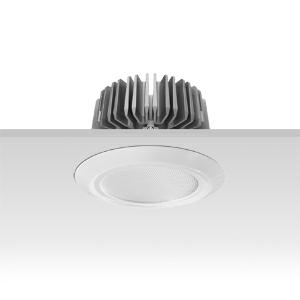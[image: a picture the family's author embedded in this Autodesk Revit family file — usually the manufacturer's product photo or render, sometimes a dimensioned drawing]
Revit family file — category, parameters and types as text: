
# Revit family: 3f_filippi_-_3f_reno_bianco_ampio_3f_filippi_-_30345_a01046_-_3f_reno_150_wh_2000-930_wide___smp_wh_e8fd
name_source: partatom
category: Lighting Fixtures
units: mm (PartAtom-declared; Revit-internal decimal feet)

## family parameters
Cut with Voids When Loaded = No
Host = Face
Light Source = No
Part Type = Normal
Room Calculation Point = No
Round Connector Dimension = Use Diameter
Shared = No

## types (1)
- 3F Filippi - 3F Reno Bianco Ampio (1 x LED, 1652 lm, 24 W, 3000 K)
    Apparent Load = 24 VA
    Approval mark = CE
    CIE Flux Codes = 73 92 98 100 100
    Color Rendering = 90
    Color Temperature = 3000 K
    Control Gear = Electronic ballast
    Default Elevation = 1800 mm
    Description = ILLUMINOTECHNICAL
Luminous efficiency 100% (DLOR 100%, ULOR 0%).
Initial luminous flux of the luminaire 1652 lm.
Direct symmetric wide distribution.
Installation Interdistance Transv.D = 1.01 x hu - Long.D = 1.00 x hu.
Tabular UGR (CIE 117 - 4H-8H; S=0.25H; 70/50/20): RUG 23.3 - 23.3.
Beam angle: 70° - 70°.
Luminous efficacy 69 lm/W.
Lifetime (L90/B10): 30000 h. (tq+25°C)
Lifetime (L85/B10): 50000 h. (tq+25°C)
Lifetime (L70/B10): 80000 h. (tq+25°C)
Sudden decreased luminous flux after 50000 hours: 0% (C0).
Photobiological safety in compliance with IEC/TR 62778: RG0 risk exempt, (IEC 62471).
In compliance with IEC/EN 62722-2-1 - IEC/EN 62717 standards.

SOURCE
Compact LED module 2000/930.
Energy efficiency class (UE 2019/2020 - UE 2019/2015): E.
CIE 13.3 Colour rendering index: CRI >90 (R9 >50%).
IES TM-30 Fidelity Index: Rf = 92 Rg = 101.
CCT nominal colour temperature 3000 K.
Colour initial tolerance (MacAdam): SDCM 3.
Zhaga Book 3 compliant.

MECHANICAL
Passive heat dissipator in die-casting aluminium, oversized, for optimum thermal management of the LED module.
Parabolic element with graduated/concentric rings in white polycarbonate.
Transparent external lens with glossy and satin differentiated surfaces, with a cooling and anti-insect system in methacrylate (PMMA).
Fastening spring clips in stainless steel.
Dimensions: diameter 176 mm, height 111 mm. Weight 0.75 kg.
IP44 protection degree for exposed part, IP20 for recessed part.
Mechanical strength to impacts IK05 (0.7 joule).
Glow-wire test resistance 650°C.

ELECTRICAL
Wiring on a separate unit.
Halogen Free electronic wiring 230V-50/60Hz, power factor 0.95, THD <25%, constant output current, SELV, class II, 1 driver.
Power of the luminaire 24 W.
ENEC - CE.
SAFE FLICKER: PstLM=<1 and SVM=<0.4 (IEC TR 61547-1 and IEC TR 63158), to ensure a more comfortable and safe light.
Luminaire compliant with EN 60598-2-22 for power supply from a centralised emergency system CPSS (Central Power Supply System), not incorporated in the luminaire - high risk areas excluded. The default power and flux are 100% in AC and 100% in DC.
Ambient temperature from 0°C to +25°C.
Temperature class T6 max 85°C.
Relative humidity UR: <85%.

INSTALLATION
Pull-up recessed fitting.
False ceiling carving: 150 mm.
All accessories dedicated to this product are available on the Catalog and on our website www.3F-Filippi.com.

ACCESSORIES
A01046 - Anti-glare microprismatic SMP diffuser in methacrylate (PMMA), locked and in line with the trim, in white polycarbonate.

APPLICATIONS
Suitable product for food production plants (HACCP), IFS (Food Version 6), BRC (GSFS Food Version 7).
Environments: architectural, commercial, exhibition areas, transit areas, corridors, shops, display windows, service areas.
In false ceilings with narrow voids.

WARNING
Luminaire designed for disposal/recycling at end-of-life.
Replaceable (LED only) light source by a professional. Replaceable control gear by a professional.
    Height = 0 mm  [stored 0 ft]
    Lamp = 1 x LED
    Lamp Light Flux = 1652 lm
    Lamp Power = 24 W
    Lamp count = 1
    Length = 176 mm
    Lifetime = 50000 h
    Luminous efficacy = 69 lm/W
    Manufacturer = 3F Filippi
    ModVariant = No
    Model = 3F Filippi - 30345+A01046 - 3F Reno 150 WH 2000-930 WIDE + SMP WH
    Mounting Place = Ceiling
    Mounting Type = Recessed
    Number of Poles = 1
    OnlyDefault = Yes
    Power Factor = 1
    Product Name = 3F Filippi - 3F Reno Bianco Ampio
    Product group = recessed luminaire
    ProductGroupID = 4
    Protection Class = Protection class II
    Protection Degree = IP 20
    RLX_Detail_Level = 1
    RLX_Emergency_Light_Flux = 0 lm
    RLX_Emergency_Type = 0
    RLX_Emergency_Type_DB = No
    RlxData = <blob elided: 84021 chars, md5=d52d28d7>
    Socket = socket
    Standby Power = 0 W
    System Light Flux = 1652 lm
    System Power = 24 W
    Type Comments = Product without accessories
    Type Image = 3ffilippi_3f_reno_150_wh_vs_smp.jpg
    URL = http://relux.com
    VarID = ---
    Voltage = 0 V
    Weight = 0.00 kg
    Width = 0 mm  [stored 0 ft]

note: [stored X ft] marks values corroborated as IEEE doubles in the binary element streams (Revit-internal decimal feet)

## geometry (parser evidence)
native form markers: Blend x4, Sweep x12
no freeform markers — native parametric forms only
